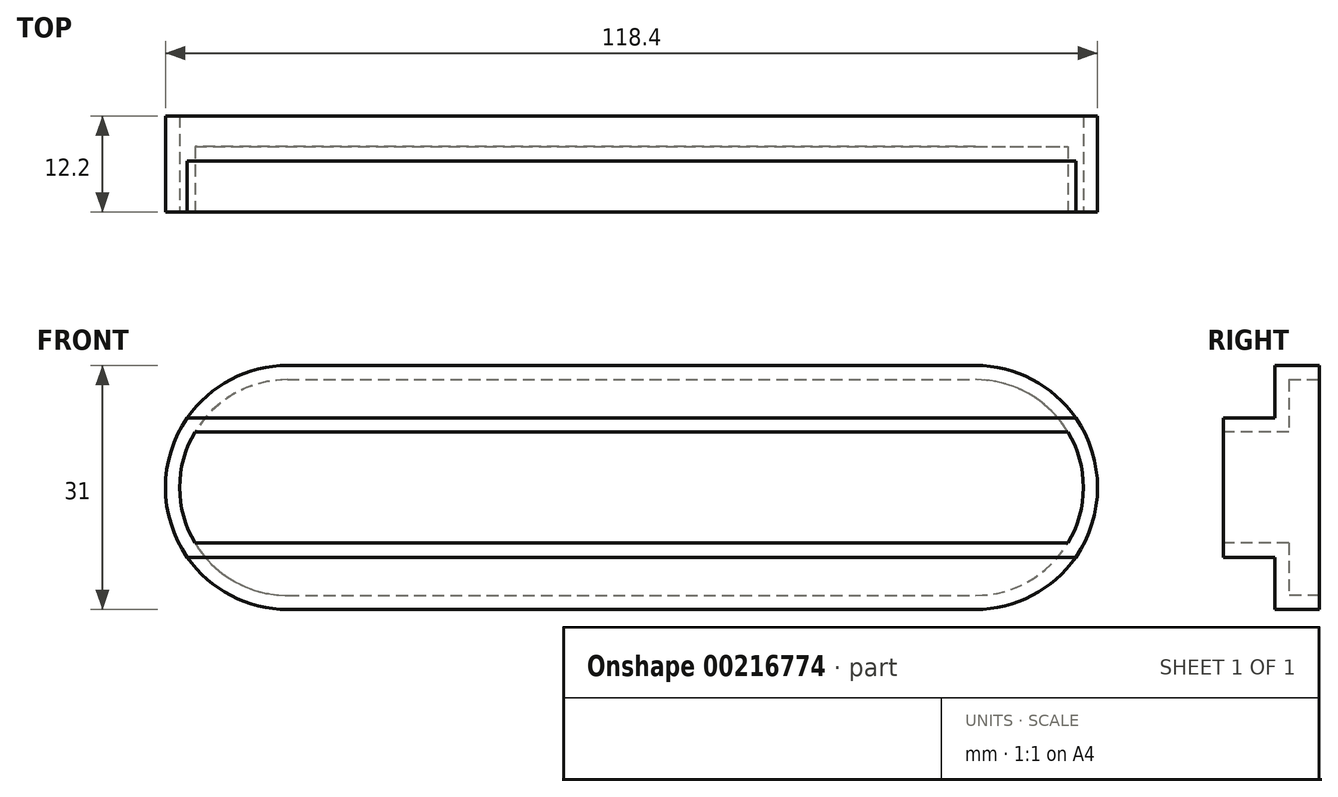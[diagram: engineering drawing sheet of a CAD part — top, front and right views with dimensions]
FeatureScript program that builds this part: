
annotation { "Feature Type Name" : "Feature", "Feature Type Description" : "" }
export const myFeature = defineFeature(function(context is Context, id is Id, definition is map)
    precondition{}
    {
        {
            var Q0;
            Q0=qCreatedBy(makeId("Front.planeOp"),FACE);
            var sketch = newSketch(context, id + "F0", { "sketchPlane" : qUnion([Q0])});
            skLineSegment(sketch, "E0.bottom", {"start": v(-43.7, 15.5) * mm, "end": v(43.7, 15.5) * mm});
            skLineSegment(sketch, "E0.top", {"start": v(-43.7, -15.5) * mm, "end": v(43.7, -15.5) * mm});
            skLineSegment(sketch, "E0.left", {"start": v(-59.2, 0) * mm, "end": v(-59.2, 0) * mm});
            skLineSegment(sketch, "E0.right", {"start": v(59.2, 0) * mm, "end": v(59.2, 0) * mm});
            skPoint(sketch, "E1", {"position": v(0, 15.5) * mm});
            skPoint(sketch, "E2", {"position": v(59.2, 0) * mm});
            skPoint(sketch, "E3.visualSharp", {"position": v(-59.2, 15.5) * mm});
            skArc(sketch, "E3.filletArc", {"start": v(-43.7, 15.5) * mm, "mid": v(-54.66, 10.96) * mm, "end": v(-59.2, 0) * mm});
            skPoint(sketch, "E4.visualSharp", {"position": v(-59.2, -15.5) * mm});
            skArc(sketch, "E4.filletArc", {"start": v(-59.2, 0) * mm, "mid": v(-54.66, -10.96) * mm, "end": v(-43.7, -15.5) * mm});
            skPoint(sketch, "E5.visualSharp", {"position": v(59.2, 15.5) * mm});
            skArc(sketch, "E5.filletArc", {"start": v(59.2, 0) * mm, "mid": v(54.66, 10.96) * mm, "end": v(43.7, 15.5) * mm});
            skPoint(sketch, "E6.visualSharp", {"position": v(59.2, -15.5) * mm});
            skArc(sketch, "E6.filletArc", {"start": v(43.7, -15.5) * mm, "mid": v(54.66, -10.96) * mm, "end": v(59.2, 0) * mm});
            skSolve(sketch);
        }
        {
            var Q0;
            Q0 = qSketchRegion(id + "F0", true);
            extrude(context, id + "F1", {"entities" : qUnion([Q0]), "oppositeDirection" : true, "depth" : 5.7 * mm});
        }
        {
            var Q0;
            Q0=qCreatedBy(makeId("Front.planeOp"),FACE);
            var sketch = newSketch(context, id + "F2", { "sketchPlane" : qUnion([Q0])});
            skLineSegment(sketch, "E7.bottom", {"start": v(-73.02, 22.64) * mm, "end": v(72.94, 22.64) * mm});
            skLineSegment(sketch, "E7.top", {"start": v(-73.02, 8.85) * mm, "end": v(72.94, 8.85) * mm});
            skLineSegment(sketch, "E7.left", {"start": v(-73.02, 22.64) * mm, "end": v(-73.02, 8.85) * mm});
            skLineSegment(sketch, "E7.right", {"start": v(72.94, 22.64) * mm, "end": v(72.94, 8.85) * mm});
            skLineSegment(sketch, "E8.bottom", {"start": v(-71.96, -8.85) * mm, "end": v(72.7, -8.85) * mm});
            skLineSegment(sketch, "E8.top", {"start": v(-71.96, -25.36) * mm, "end": v(72.7, -25.36) * mm});
            skLineSegment(sketch, "E8.left", {"start": v(-71.96, -8.85) * mm, "end": v(-71.96, -25.36) * mm});
            skLineSegment(sketch, "E8.right", {"start": v(72.7, -8.85) * mm, "end": v(72.7, -25.36) * mm});
            skSolve(sketch);
        }
        {
            var Q0;
            Q0 = qSketchRegion(id + "F0", true);
            extrude(context, id + "F3", {"entities" : qUnion([Q0]), "operationType" : NewBodyOperationType.ADD, "depth" : 6.5 * mm});
        }
        {
            var Q0;
            Q0 = qSketchRegion(id + "F2", true);
            extrude(context, id + "F4", {"entities" : qUnion([Q0]), "operationType" : NewBodyOperationType.REMOVE, "depth" : 25 * mm});
        }
        {
            var Q0;
            Q0=makeQuery(id+"F1.opExtrude","CAP_FACE",FACE,{"disambiguationData":[OSD([sQuery(id+"F0.wireOp",EDGE,"E0.bottom"),sQuery(id+"F0.wireOp",EDGE,"E0.top"),sQuery(id+"F0.wireOp",EDGE,"E3.filletArc"),sQuery(id+"F0.wireOp",EDGE,"E4.filletArc"),sQuery(id+"F0.wireOp",EDGE,"E5.filletArc"),sQuery(id+"F0.wireOp",EDGE,"E6.filletArc")])],"isStart":false});
            var Q1;
            Q1=makeQuery(id+"F3.opExtrude","CAP_FACE",FACE,{"disambiguationData":[OSD([sQuery(id+"F0.wireOp",EDGE,"E0.bottom"),sQuery(id+"F0.wireOp",EDGE,"E0.top"),sQuery(id+"F0.wireOp",EDGE,"E3.filletArc"),sQuery(id+"F0.wireOp",EDGE,"E4.filletArc"),sQuery(id+"F0.wireOp",EDGE,"E5.filletArc"),sQuery(id+"F0.wireOp",EDGE,"E6.filletArc")])],"isStart":false});
            shell(context, id + "F5", {"entities" : qUnion([Q0, Q1]), "thickness" : 1.8 * mm});
        }
    });
